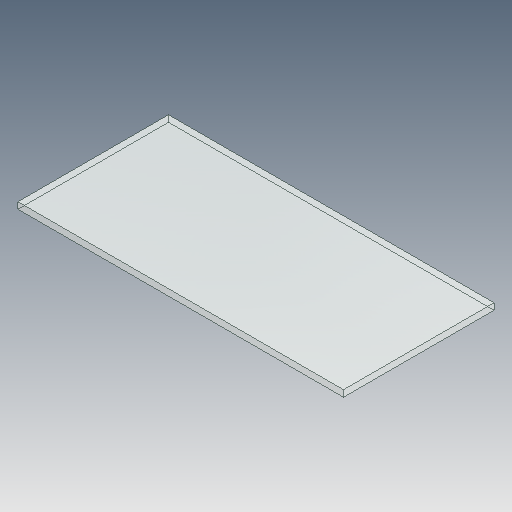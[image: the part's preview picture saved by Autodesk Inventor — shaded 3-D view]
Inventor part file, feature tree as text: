
AUTODESK INVENTOR PART (.ipt)
format: ipt  version: 2020.3 (Build 243373010, 373A)  size: 89,088 bytes
history: native  units: mm
features: extrude x1, sketch x1
ambient origin geometry x8: Origin, YZ Plane, XZ Plane, XY Plane, X Axis, Y Axis, Z Axis, Center Point
bodies: Solid1 (feature_tree)
feature tree (2):
  extrude  "Extrusion1"  Depth=92.5mm
  sketch  "Sketch1"  dims[d0=200.0mm d1=92.5mm d2=4.0mm d3=0.0mm]
